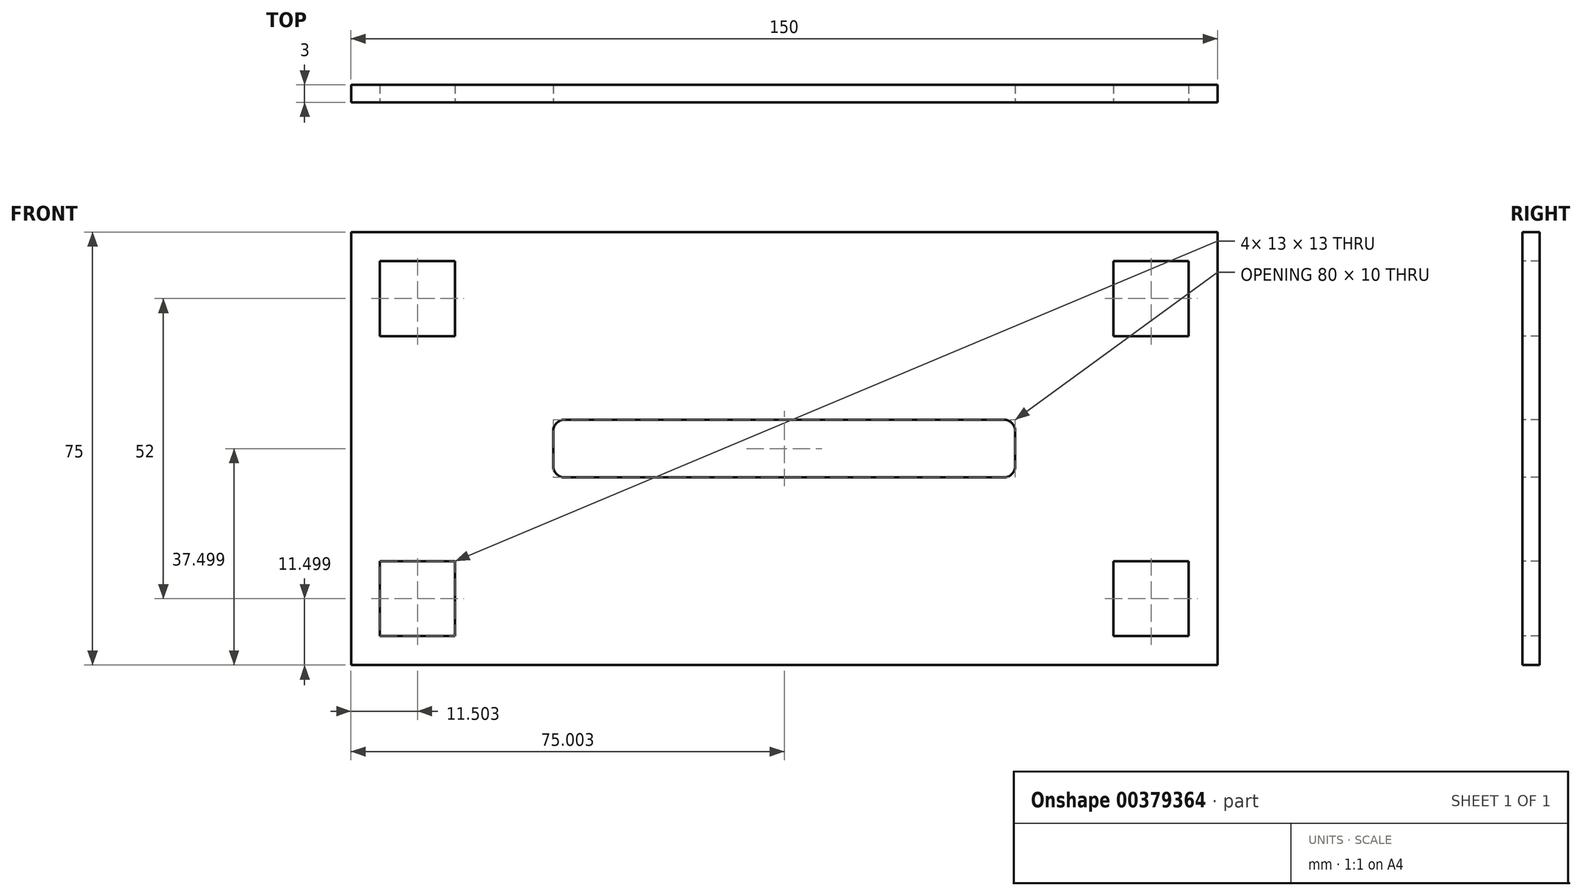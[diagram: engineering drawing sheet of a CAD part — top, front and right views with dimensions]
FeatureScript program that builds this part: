
annotation { "Feature Type Name" : "Feature", "Feature Type Description" : "" }
export const myFeature = defineFeature(function(context is Context, id is Id, definition is map)
    precondition{}
    {
        {
            var Q0;
            Q0=qCreatedBy(makeId("Front.planeOp"),FACE);
            var sketch = newSketch(context, id + "F0", { "sketchPlane" : qUnion([Q0])});
            skLineSegment(sketch, "E0.bottom", {"start": v(-43.02, 83.85) * mm, "end": v(106.98, 83.85) * mm});
            skLineSegment(sketch, "E0.top", {"start": v(-43.02, 8.85) * mm, "end": v(106.98, 8.85) * mm});
            skLineSegment(sketch, "E0.left", {"start": v(-43.02, 83.85) * mm, "end": v(-43.02, 8.85) * mm});
            skLineSegment(sketch, "E0.right", {"start": v(106.98, 83.85) * mm, "end": v(106.98, 8.85) * mm});
            skSolve(sketch);
        }
        {
            var Q0;
            Q0=qSketchRegion(id+"F0",true);
            extrude(context, id + "F1", {"entities" : qUnion([Q0]), "depth" : 3 * mm, "offsetDistance" : 25 * mm});
        }
        {
            var Q0;
            Q0=makeQuery(id+"F1.opExtrude","CAP_FACE",FACE,{"disambiguationData":[OSD([sQuery(id+"F0.wireOp",EDGE,"E0.bottom"),sQuery(id+"F0.wireOp",EDGE,"E0.top"),sQuery(id+"F0.wireOp",EDGE,"E0.left"),sQuery(id+"F0.wireOp",EDGE,"E0.right")])],"isStart":false});
            var sketch = newSketch(context, id + "F2", { "sketchPlane" : qUnion([Q0])});
            skLineSegment(sketch, "E1.bottom", {"start": v(-38.02, 78.85) * mm, "end": v(-25.02, 78.85) * mm});
            skLineSegment(sketch, "E1.top", {"start": v(-38.02, 65.85) * mm, "end": v(-25.02, 65.85) * mm});
            skLineSegment(sketch, "E1.left", {"start": v(-38.02, 78.85) * mm, "end": v(-38.02, 65.85) * mm});
            skLineSegment(sketch, "E1.right", {"start": v(-25.02, 78.85) * mm, "end": v(-25.02, 65.85) * mm});
            skLineSegment(sketch, "E2.bottom", {"start": v(-38.02, 26.85) * mm, "end": v(-25.02, 26.85) * mm});
            skLineSegment(sketch, "E2.top", {"start": v(-38.02, 13.85) * mm, "end": v(-25.02, 13.85) * mm});
            skLineSegment(sketch, "E2.left", {"start": v(-38.02, 26.85) * mm, "end": v(-38.02, 13.85) * mm});
            skLineSegment(sketch, "E2.right", {"start": v(-25.02, 26.85) * mm, "end": v(-25.02, 13.85) * mm});
            skLineSegment(sketch, "E3.bottom", {"start": v(88.98, 26.85) * mm, "end": v(101.98, 26.85) * mm});
            skLineSegment(sketch, "E3.top", {"start": v(88.98, 13.85) * mm, "end": v(101.98, 13.85) * mm});
            skLineSegment(sketch, "E3.left", {"start": v(88.98, 26.85) * mm, "end": v(88.98, 13.85) * mm});
            skLineSegment(sketch, "E3.right", {"start": v(101.98, 26.85) * mm, "end": v(101.98, 13.85) * mm});
            skLineSegment(sketch, "E4.bottom", {"start": v(101.98, 78.85) * mm, "end": v(88.98, 78.85) * mm});
            skLineSegment(sketch, "E4.top", {"start": v(101.98, 65.85) * mm, "end": v(88.98, 65.85) * mm});
            skLineSegment(sketch, "E4.left", {"start": v(101.98, 78.85) * mm, "end": v(101.98, 65.85) * mm});
            skLineSegment(sketch, "E4.right", {"start": v(88.98, 78.85) * mm, "end": v(88.98, 65.85) * mm});
            skLineSegment(sketch, "E5.bottom", {"start": v(-6.02, 51.35) * mm, "end": v(69.98, 51.35) * mm});
            skLineSegment(sketch, "E5.top", {"start": v(-6.02, 41.35) * mm, "end": v(69.98, 41.35) * mm});
            skLineSegment(sketch, "E5.left", {"start": v(-8.02, 49.35) * mm, "end": v(-8.02, 43.35) * mm});
            skLineSegment(sketch, "E5.right", {"start": v(71.98, 49.35) * mm, "end": v(71.98, 43.35) * mm});
            skPoint(sketch, "E6.visualSharp", {"position": v(-8.02, 51.35) * mm});
            skArc(sketch, "E6.filletArc", {"start": v(-6.02, 51.35) * mm, "mid": v(-7.43, 50.76) * mm, "end": v(-8.02, 49.35) * mm});
            skPoint(sketch, "E7.visualSharp", {"position": v(-8.02, 41.35) * mm});
            skArc(sketch, "E7.filletArc", {"start": v(-8.02, 43.35) * mm, "mid": v(-7.43, 41.93) * mm, "end": v(-6.02, 41.35) * mm});
            skPoint(sketch, "E8.visualSharp", {"position": v(71.98, 51.35) * mm});
            skArc(sketch, "E8.filletArc", {"start": v(71.98, 49.35) * mm, "mid": v(71.4, 50.76) * mm, "end": v(69.98, 51.35) * mm});
            skPoint(sketch, "E9.visualSharp", {"position": v(71.98, 41.35) * mm});
            skArc(sketch, "E9.filletArc", {"start": v(69.98, 41.35) * mm, "mid": v(71.4, 41.93) * mm, "end": v(71.98, 43.35) * mm});
            skSolve(sketch);
        }
        {
            var Q0;
            Q0=qSketchRegion(id+"F2",true);
            extrude(context, id + "F3", {"entities" : qUnion([Q0]), "operationType" : NewBodyOperationType.REMOVE, "oppositeDirection" : true, "depth" : 4 * mm, "offsetDistance" : 25 * mm});
        }
    });
